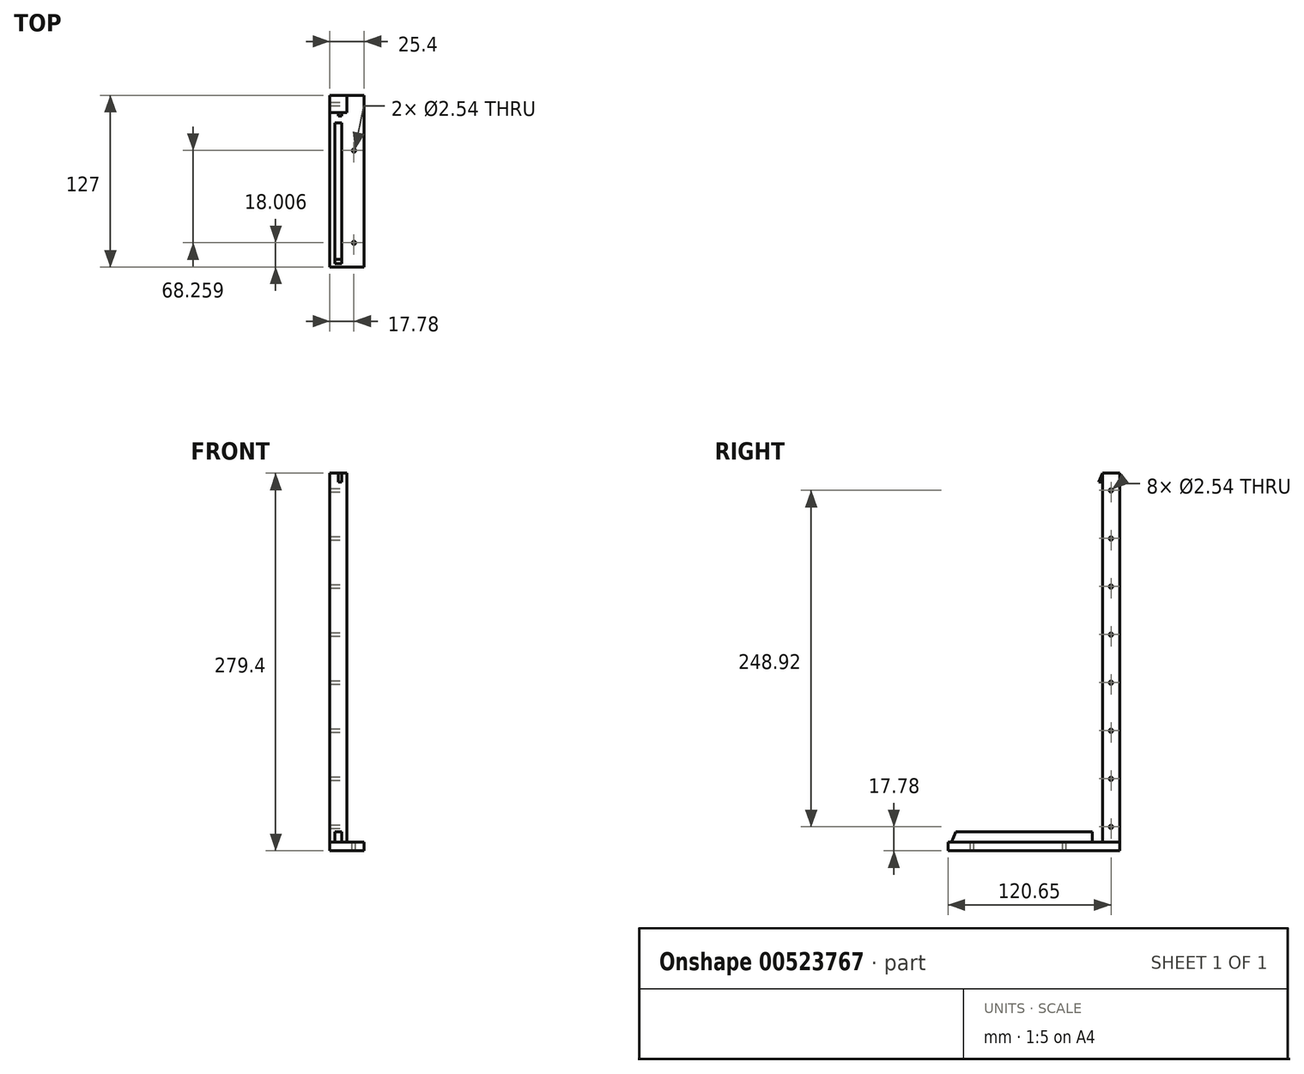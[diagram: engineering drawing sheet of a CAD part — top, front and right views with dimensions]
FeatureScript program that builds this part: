
annotation { "Feature Type Name" : "Feature", "Feature Type Description" : "" }
export const myFeature = defineFeature(function(context is Context, id is Id, definition is map)
    precondition{}
    {
        {
            var Q0;
            Q0=qCreatedBy(makeId("Top.planeOp"),FACE);
            var sketch = newSketch(context, id + "F0", { "sketchPlane" : qUnion([Q0])});
            skLineSegment(sketch, "E0.bottom", {"start": v(0, 0) * mm, "end": v(-25.4, 0) * mm});
            skLineSegment(sketch, "E0.top", {"start": v(0, 127) * mm, "end": v(-25.4, 127) * mm});
            skLineSegment(sketch, "E0.left", {"start": v(0, 0) * mm, "end": v(0, 127) * mm});
            skLineSegment(sketch, "E0.right", {"start": v(-25.4, 0) * mm, "end": v(-25.4, 127) * mm});
            skSolve(sketch);
        }
        {
            var Q0;
            Q0=makeQuery(id+"F0.imprint","IMPRINT",FACE,{"disambiguationData":[TD([[makeQuery(id+"F0.imprint","IMPRINT",EDGE,{"derivedFrom":sQuery(id+"F0.wireOp",EDGE,"E0.bottom")}),-1.0]])]});
            extrude(context, id + "F1", {"entities" : qUnion([Q0]), "depth" : 6.35 * mm, "offsetDistance" : 25.4 * mm});
        }
        {
            var Q0;
            Q0=makeQuery(id+"F1.opExtrude","CAP_FACE",FACE,{"disambiguationData":[OSD([sQuery(id+"F0.wireOp",EDGE,"E0.bottom"),sQuery(id+"F0.wireOp",EDGE,"E0.top"),sQuery(id+"F0.wireOp",EDGE,"E0.left"),sQuery(id+"F0.wireOp",EDGE,"E0.right")])],"isStart":false});
            var sketch = newSketch(context, id + "F2", { "sketchPlane" : qUnion([Q0])});
            skLineSegment(sketch, "E1.bottom", {"start": v(-25.4, 127) * mm, "end": v(-12.7, 127) * mm});
            skLineSegment(sketch, "E1.top", {"start": v(-25.4, 114.3) * mm, "end": v(-12.7, 114.3) * mm});
            skLineSegment(sketch, "E1.left", {"start": v(-25.4, 127) * mm, "end": v(-25.4, 114.3) * mm});
            skLineSegment(sketch, "E1.right", {"start": v(-12.7, 127) * mm, "end": v(-12.7, 114.3) * mm});
            skSolve(sketch);
        }
        {
            var Q0;
            Q0=makeQuery(id+"F2.imprint","IMPRINT",FACE,{"disambiguationData":[TD([[makeQuery(id+"F2.imprint","IMPRINT",EDGE,{"derivedFrom":sQuery(id+"F2.wireOp",EDGE,"E1.bottom")}),1.0]])]});
            extrude(context, id + "F3", {"entities" : qUnion([Q0]), "operationType" : NewBodyOperationType.ADD, "depth" : 273.05 * mm, "offsetDistance" : 25.4 * mm});
        }
        {
            var Q0;
            Q0=makeQuery(id+"F3.opExtrude","SWEPT_FACE",FACE,{"disambiguationData":[OSD([sQuery(id+"F2.wireOp",EDGE,"E1.top")])]});
            var sketch = newSketch(context, id + "F4", { "sketchPlane" : qUnion([Q0])});
            skLineSegment(sketch, "E2", {"start": v(-19.05, 279.4) * mm, "end": v(-19.05, 272.87) * mm});
            skLineSegment(sketch, "E3", {"start": v(-19.05, 272.87) * mm, "end": v(-21.59, 272.87) * mm});
            skLineSegment(sketch, "E4.top", {"start": v(-19.05, 279.4) * mm, "end": v(-21.59, 279.4) * mm});
            skLineSegment(sketch, "E4.left", {"start": v(-19.05, 272.87) * mm, "end": v(-19.05, 279.4) * mm});
            skLineSegment(sketch, "E4.right", {"start": v(-21.59, 272.87) * mm, "end": v(-21.59, 279.4) * mm});
            skSolve(sketch);
        }
        {
            var Q0;
            Q0=makeQuery(id+"F4.imprint","IMPRINT",FACE,{"disambiguationData":[TD([[makeQuery(id+"F4.imprint","IMPRINT",EDGE,{"derivedFrom":sQuery(id+"F4.wireOp",EDGE,"E3")}),-1.0]])]});
            extrude(context, id + "F5", {"entities" : qUnion([Q0]), "operationType" : NewBodyOperationType.ADD, "depth" : 25.4 * mm, "offsetDistance" : 25.4 * mm});
        }
        {
            var Q0;
            Q0=makeQuery(id+"F5.opExtrude","SWEPT_FACE",FACE,{"disambiguationData":[OSD([sQuery(id+"F4.wireOp",EDGE,"E4.right")])]});
            var sketch = newSketch(context, id + "F6", { "sketchPlane" : qUnion([Q0])});
            skLineSegment(sketch, "E5", {"start": v(-114.3, 279.4) * mm, "end": v(0, 0) * mm});
            skLineSegment(sketch, "E6", {"start": v(0, 0) * mm, "end": v(-114.3, 0) * mm});
            skLineSegment(sketch, "E7", {"start": v(-114.3, 0) * mm, "end": v(-114.3, 279.4) * mm});
            skLineSegment(sketch, "E8", {"start": v(-114.3, 0) * mm, "end": v(-96.32, 0) * mm});
            skLineSegment(sketch, "E9", {"start": v(-114.3, 0) * mm, "end": v(-114.3, 6.35) * mm});
            skLineSegment(sketch, "E10", {"start": v(-114.3, 6.35) * mm, "end": v(-106.68, 6.35) * mm});
            skLineSegment(sketch, "E11", {"start": v(-106.68, 6.35) * mm, "end": v(-106.68, 13.97) * mm});
            skLineSegment(sketch, "E12", {"start": v(-106.68, 13.97) * mm, "end": v(-5.71, 13.97) * mm});
            skLineSegment(sketch, "E13", {"start": v(-5.71, 13.97) * mm, "end": v(-13.34, 13.97) * mm});
            skLineSegment(sketch, "E14", {"start": v(-114.3, 279.4) * mm, "end": v(-114.3, 263.18) * mm});
            skLineSegment(sketch, "E15", {"start": v(-106.68, 13.97) * mm, "end": v(-106.68, 217.25) * mm});
            skLineSegment(sketch, "E16", {"start": v(-106.68, 217.25) * mm, "end": v(-106.68, 237.58) * mm});
            skLineSegment(sketch, "E17", {"start": v(-106.68, 237.58) * mm, "end": v(-13.33, 13.97) * mm});
            skSolve(sketch);
        }
        {
            var Q0;
            {var subQ5=sQuery(id+"F6.wireOp",EDGE,"E7");Q0=makeQuery(id+"F6.imprint","IMPRINT",FACE,{"disambiguationData":[TD([[makeQuery(id+"F6.imprint","IMPRINT",EDGE,{"derivedFrom":subQ5}),-1.0]])]});}
            var Q1;
            {var subQ0=sQuery(id+"F6.wireOp",EDGE,"E6");Q1=makeQuery(id+"F6.imprint","IMPRINT",FACE,{"disambiguationData":[TD([[makeQuery(id+"F6.imprint","IMPRINT",EDGE,{"derivedFrom":subQ0}),-1.0]])]});}
            extrude(context, id + "F7", {"entities" : qUnion([Q0, Q1]), "operationType" : NewBodyOperationType.ADD, "oppositeDirection" : true, "depth" : 5.08 * mm, "offsetDistance" : 25.4 * mm});
        }
        {
            var Q0;
            Q0=makeQuery(id+"F5.opExtrude","CAP_FACE",FACE,{"disambiguationData":[OSD([sQuery(id+"F4.wireOp",EDGE,"E3"),sQuery(id+"F4.wireOp",EDGE,"E4.top"),sQuery(id+"F4.wireOp",EDGE,"E4.left"),sQuery(id+"F4.wireOp",EDGE,"E4.right")])],"isStart":false});
            extrude(context, id + "F8", {"entities" : qUnion([Q0]), "operationType" : NewBodyOperationType.REMOVE, "oppositeDirection" : true, "depth" : 25.4 * mm, "offsetDistance" : 25.4 * mm});
        }
        {
            var Q0;
            Q0=makeQuery(id+"F1.opExtrude","CAP_FACE",FACE,{"disambiguationData":[OSD([sQuery(id+"F0.wireOp",EDGE,"E0.bottom"),sQuery(id+"F0.wireOp",EDGE,"E0.top"),sQuery(id+"F0.wireOp",EDGE,"E0.left"),sQuery(id+"F0.wireOp",EDGE,"E0.right")])],"isStart":false});
            var sketch = newSketch(context, id + "F9", { "sketchPlane" : qUnion([Q0])});
            skLineSegment(sketch, "E18", {"start": v(0, 18) * mm, "end": v(-7.62, 18) * mm});
            skLineSegment(sketch, "E19", {"start": v(-7.62, 18) * mm, "end": v(-7.62, 86.27) * mm});
            skCircle(sketch, "E20", {"center": v(-7.62, 86.27) * mm, "radius": 1.27 * mm});
            skCircle(sketch, "E21", {"center": v(-7.62, 18) * mm, "radius": 1.27 * mm});
            skSolve(sketch);
        }
        {
            var Q0;
            Q0=makeQuery(id+"F9.imprint","IMPRINT",FACE,{"disambiguationData":[TD([[makeQuery(id+"F9.imprint","IMPRINT",EDGE,{"derivedFrom":sQuery(id+"F9.wireOp",EDGE,"E20")}),1.0]])]});
            var Q1;
            {var subQ0=sQuery(id+"F9.wireOp",EDGE,"E19");var subQ1=sQuery(id+"F9.wireOp",EDGE,"E18");var subQ2=makeQuery(id+"F9.imprint","INTERSECT",VERTEX,{"derivedFrom":[subQ1,subQ0]});Q1=makeQuery(id+"F9.imprint","IMPRINT",FACE,{"disambiguationData":[TD([[makeQuery(id+"F9.imprint","IMPRINT",EDGE,{"disambiguationData":[TD([[subQ2,1.0]])],"derivedFrom":subQ1}),1.0]])]});}
            var Q2;
            {var subQ0=sQuery(id+"F9.wireOp",EDGE,"E19");var subQ1=sQuery(id+"F9.wireOp",EDGE,"E18");var subQ2=makeQuery(id+"F9.imprint","INTERSECT",VERTEX,{"derivedFrom":[subQ1,subQ0]});Q2=makeQuery(id+"F9.imprint","IMPRINT",FACE,{"disambiguationData":[TD([[makeQuery(id+"F9.imprint","IMPRINT",EDGE,{"disambiguationData":[TD([[subQ2,1.0]])],"derivedFrom":subQ1}),-1.0]])]});}
            extrude(context, id + "F10", {"entities" : qUnion([Q0, Q1, Q2]), "operationType" : NewBodyOperationType.REMOVE, "oppositeDirection" : true, "depth" : 25.4 * mm, "offsetDistance" : 25.4 * mm});
        }
        {
            var Q0;
            Q0=makeQuery(id+"F3.opExtrude","SWEPT_FACE",FACE,{"disambiguationData":[OSD([sQuery(id+"F2.wireOp",EDGE,"E1.right")])]});
            var sketch = newSketch(context, id + "F11", { "sketchPlane" : qUnion([Q0])});
            skLineSegment(sketch, "E22", {"start": v(120.65, 279.4) * mm, "end": v(120.65, 266.7) * mm});
            skCircle(sketch, "E23", {"center": v(120.65, 266.7) * mm, "radius": 1.27 * mm});
            skCircle(sketch, "E24.0.1.0", {"center": v(120.65, 231.14) * mm, "radius": 1.27 * mm});
            skCircle(sketch, "E24.0.2.0", {"center": v(120.65, 195.58) * mm, "radius": 1.27 * mm});
            skCircle(sketch, "E24.0.3.0", {"center": v(120.65, 160.02) * mm, "radius": 1.27 * mm});
            skCircle(sketch, "E24.0.4.0", {"center": v(120.65, 124.46) * mm, "radius": 1.27 * mm});
            skCircle(sketch, "E24.0.5.0", {"center": v(120.65, 88.9) * mm, "radius": 1.27 * mm});
            skCircle(sketch, "E24.0.6.0", {"center": v(120.65, 53.34) * mm, "radius": 1.27 * mm});
            skCircle(sketch, "E24.0.7.0", {"center": v(120.65, 17.78) * mm, "radius": 1.27 * mm});
            skLineSegment(sketch, "E24.direction1", {"start": v(120.65, 266.7) * mm, "end": v(146.05, 266.7) * mm, "construction": true});
            skLineSegment(sketch, "E24.direction2", {"start": v(120.65, 266.7) * mm, "end": v(120.65, 231.14) * mm, "construction": true});
            skSolve(sketch);
        }
        {
            var Q0;
            Q0=makeQuery(id+"F11.imprint","IMPRINT",FACE,{"disambiguationData":[TD([[makeQuery(id+"F11.imprint","IMPRINT",EDGE,{"derivedFrom":sQuery(id+"F11.wireOp",EDGE,"E23")}),1.0]])]});
            var Q1;
            Q1=makeQuery(id+"F11.imprint","IMPRINT",FACE,{"disambiguationData":[TD([[makeQuery(id+"F11.imprint","IMPRINT",EDGE,{"derivedFrom":sQuery(id+"F11.wireOp",EDGE,"E24.0.1.0")}),1.0]])]});
            var Q2;
            Q2=makeQuery(id+"F11.imprint","IMPRINT",FACE,{"disambiguationData":[TD([[makeQuery(id+"F11.imprint","IMPRINT",EDGE,{"derivedFrom":sQuery(id+"F11.wireOp",EDGE,"E24.0.2.0")}),1.0]])]});
            var Q3;
            Q3=makeQuery(id+"F11.imprint","IMPRINT",FACE,{"disambiguationData":[TD([[makeQuery(id+"F11.imprint","IMPRINT",EDGE,{"derivedFrom":sQuery(id+"F11.wireOp",EDGE,"E24.0.3.0")}),1.0]])]});
            var Q4;
            Q4=makeQuery(id+"F11.imprint","IMPRINT",FACE,{"disambiguationData":[TD([[makeQuery(id+"F11.imprint","IMPRINT",EDGE,{"derivedFrom":sQuery(id+"F11.wireOp",EDGE,"E24.0.4.0")}),1.0]])]});
            var Q5;
            Q5=makeQuery(id+"F11.imprint","IMPRINT",FACE,{"disambiguationData":[TD([[makeQuery(id+"F11.imprint","IMPRINT",EDGE,{"derivedFrom":sQuery(id+"F11.wireOp",EDGE,"E24.0.5.0")}),1.0]])]});
            var Q6;
            Q6=makeQuery(id+"F11.imprint","IMPRINT",FACE,{"disambiguationData":[TD([[makeQuery(id+"F11.imprint","IMPRINT",EDGE,{"derivedFrom":sQuery(id+"F11.wireOp",EDGE,"E24.0.6.0")}),1.0]])]});
            var Q7;
            Q7=makeQuery(id+"F11.imprint","IMPRINT",FACE,{"disambiguationData":[TD([[makeQuery(id+"F11.imprint","IMPRINT",EDGE,{"derivedFrom":sQuery(id+"F11.wireOp",EDGE,"E24.0.7.0")}),1.0]])]});
            extrude(context, id + "F12", {"entities" : qUnion([Q0, Q1, Q2, Q3, Q4, Q5, Q6, Q7]), "operationType" : NewBodyOperationType.REMOVE, "oppositeDirection" : true, "depth" : 25.4 * mm, "offsetDistance" : 25.4 * mm});
        }
    });
